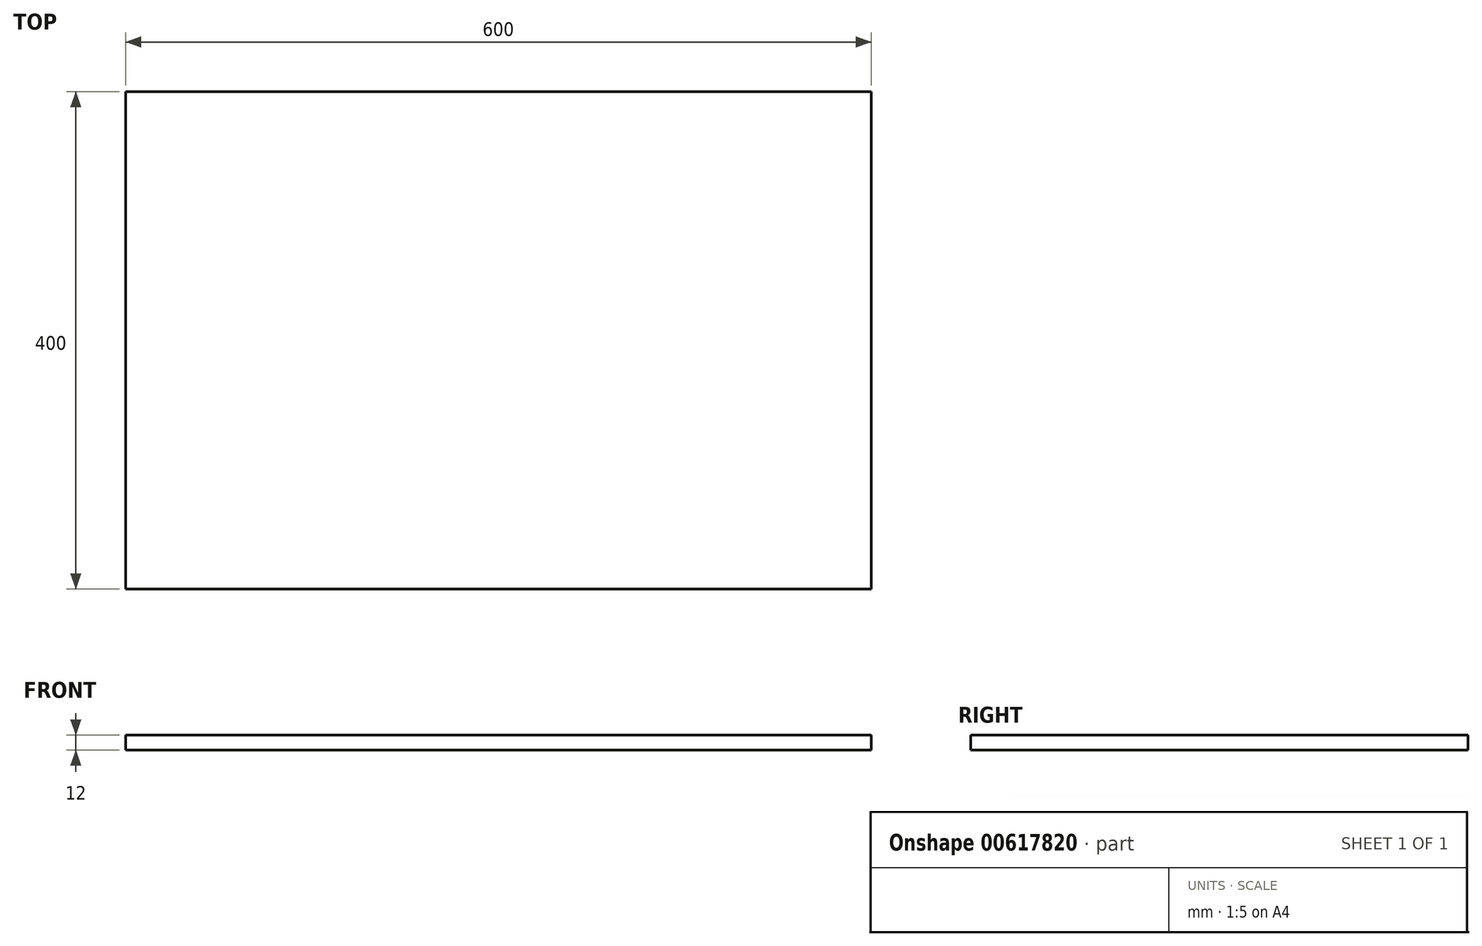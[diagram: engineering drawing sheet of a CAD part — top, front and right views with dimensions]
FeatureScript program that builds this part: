
annotation { "Feature Type Name" : "Feature", "Feature Type Description" : "" }
export const myFeature = defineFeature(function(context is Context, id is Id, definition is map)
    precondition{}
    {
        {
            var Q0;
            Q0=qCreatedBy(makeId("Top.planeOp"),FACE);
            var sketch = newSketch(context, id + "F0", { "sketchPlane" : qUnion([Q0])});
            skLineSegment(sketch, "E0.bottom", {"start": v(-297.86, 195.64) * mm, "end": v(302.14, 195.64) * mm});
            skLineSegment(sketch, "E0.top", {"start": v(-297.86, -204.36) * mm, "end": v(302.14, -204.36) * mm});
            skLineSegment(sketch, "E0.left", {"start": v(-297.86, 195.64) * mm, "end": v(-297.86, -204.36) * mm});
            skLineSegment(sketch, "E0.right", {"start": v(302.14, 195.64) * mm, "end": v(302.14, -204.36) * mm});
            skSolve(sketch);
        }
        {
            var Q0;
            Q0 = qSketchRegion(id + "F0", true);
            extrude(context, id + "F1", {"entities" : qUnion([Q0]), "depth" : 12 * mm, "offsetDistance" : 25 * mm});
        }
    });
